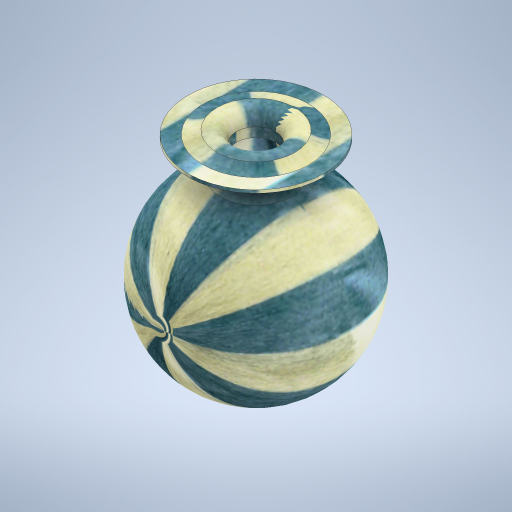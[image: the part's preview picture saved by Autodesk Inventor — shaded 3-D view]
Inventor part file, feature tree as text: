
AUTODESK INVENTOR PART (.ipt)
format: ipt  version: 2023 (Build 270158030, 158C)  size: 539,136 bytes
history: native  units: in
note: dims shown in document units (in); Inventor stores cm internally (conversion verified against a paired STEP export)
features: revolve x1, sketch x1
ambient origin geometry x8: Origin, YZ Plane, XZ Plane, XY Plane, X Axis, Y Axis, Z Axis, Center Point
bodies: Solid1 (feature_tree)
feature tree (2):
  revolve  "Revolution1"  Angle=90.0deg
  sketch  "Sketch1"  dims[d0=6.0in d4=90.0deg d8=4.5in d9=0.85in d10=0.1in d11=3.1in d13=1.0in d14=0.45in d15=0.7in d16=1.5in d18=3.5in]
